FCSTD DOCUMENT  (FreeCAD 0.19R24276 (Git))
Label: Out_gear
License: All rights reserved
LicenseURL: http://en.wikipedia.org/wiki/All_rights_reserved
objects: Sketcher::SketchObject×1, PartDesign::FeaturePython×1, PartDesign::Pocket×1, PartDesign::Body×1, Part::Cylinder×1, Part::FeaturePython×1, Part::Cut×1
note: 8 computed .brp shape members not serialized (recipe doc carries the construction recipe); baked Part::Feature solids carry a one-line shape summary decoded from their .brp

FEATURE [Sketcher::SketchObject] Sketch
  FullyConstrained = true
  MapMode = 5
  Support = -> [XY_Plane]
  sketch-geometry (1):
    g0: Circle CenterX=0 CenterY=0 CenterZ=0 NormalX=0 NormalY=0 NormalZ=1 AngleXU=0 Radius=92.75
  constraints (2):
    c: Coincident(g0,g-1)
    c: Diameter(g0) = 185.5
FEATURE [PartDesign::FeaturePython] timinggear  # WARN: FeaturePython — macro-defined, semantics opaque (R4)
  AttacherType = Attacher::AttachEngine3D
  h = 0.75
  height = 8
  offset = 0.4
  pitch = 2
  r0 = 0.555
  r1 = 1
  rs = 0.15
  teeth = 295
  type = 0
  u = 0.254
  version = 0.0.3
FEATURE [PartDesign::Pocket] Pocket
  BaseFeature = -> timinggear
  Length = 5
  Length2 = 100
  Profile = -> Sketch
  Reversed = true
  Type = 1
FEATURE [PartDesign::Body] Body
  Group = -> [Sketch,timinggear,Pocket]
  Origin = -> Origin
  Tip = -> Pocket
FEATURE [Part::Cylinder] Cylinder  label="Цилиндр"
  Angle = 360
  AttacherType = Attacher::AttachEngine3D
  Height = 8
  Radius = 92.75
FEATURE [Part::FeaturePython] involutegear  # WARN: FeaturePython — macro-defined, semantics opaque (R4)
  AttacherType = Attacher::AttachEngine3D
  backlash = 0
  beta = 0
  clearance = 0.25
  da = 178
  df = 173.5
  double_helix = false
  dw = 176
  head = 0
  height = 8
  module = 1
  numpoints = 6
  pressure_angle = 20
  properties_from_tool = false
  reversed_backlash = false
  shift = 0
  simple = false
  teeth = 176
  transverse_pitch = 3.14159
  undercut = false
  version = 0.0.3
FEATURE [Part::Cut] Cut
  Base = -> Cylinder
  Tool = -> involutegear
